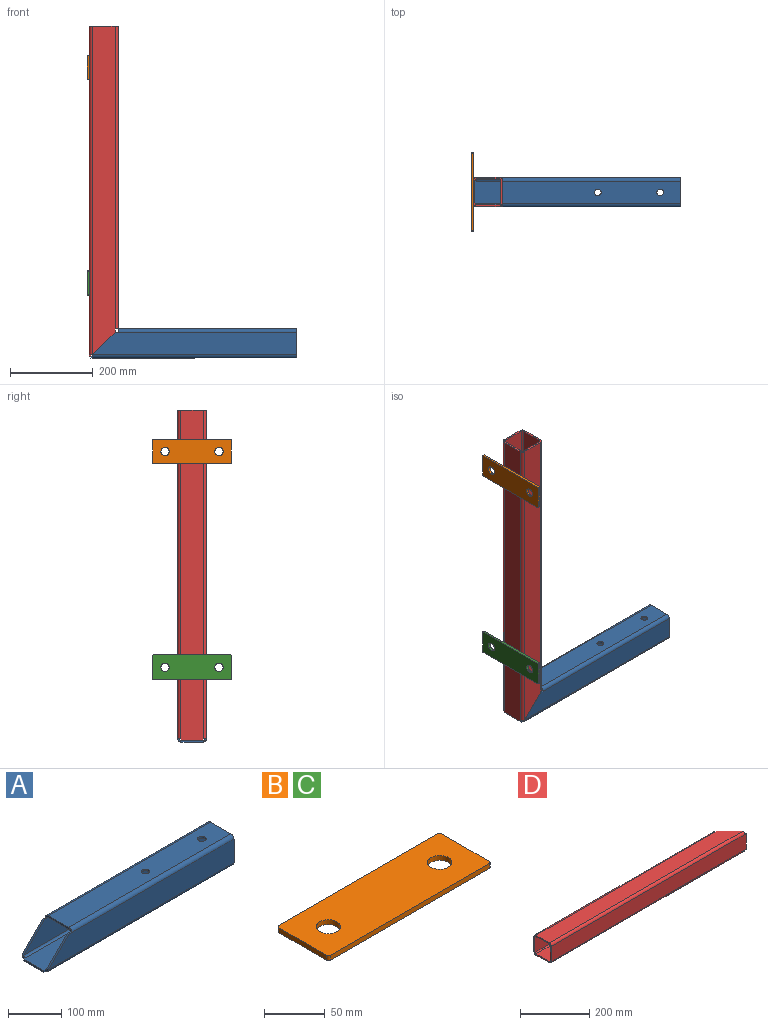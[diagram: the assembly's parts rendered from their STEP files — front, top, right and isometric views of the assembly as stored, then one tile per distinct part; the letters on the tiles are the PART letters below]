
ASSEMBLY  parts=4 mates=2
PART A: 40 faces, bbox 496x70x70 mm
  f0: plane 54x4mm, normal (1,0,0), area 216mm2, adj f3,f4,f32,f36
  f1: plane 8x4mm, normal (0,0,1), area 32mm2, adj f2,f3,f4,f33
  f2: plane 54x54mm, normal (-0.71,0,0.71), area 305.5mm2, adj f1,f3,f4,f37
  f3: plane 492x54mm, normal (0,-1,0), area 25110mm2, adj f0,f1,f2,f34,f38
  f4: plane 492x54mm, normal (0,1,0), area 25110mm2, adj f0,f1,f2,f35,f39
  f5: plane 4x4mm, normal (0,1,0), area 16mm2, adj f8,f11,f12,f28
  f6: plane 54x4mm, normal (1,0,0), area 216mm2, adj f11,f12,f29,f36
  f7: plane 4x4mm, normal (0,-1,0), area 16mm2, adj f8,f11,f12,f37
  f8: plane 54x4mm, normal (-1,0,0), area 216mm2, adj f5,f7,f11,f12
  f9: cylinder r=8mm len=16mm, axis (0,0,1), area 201.1mm2, adj f11,f12
  f10: cylinder r=8mm len=16mm, axis (0,0,1), area 201.1mm2, adj f11,f12
  f11: plane 496x54mm, normal (0,0,-1), area 26381.9mm2, adj f5,f6,f7,f8,f9,f10,f30,f38
  f12: plane 496x54mm, normal (0,0,1), area 26381.9mm2, adj f5,f6,f7,f8,f9,f10,f31,f39
  f13: plane 54x4mm, normal (1,0,0), area 216mm2, adj f17,f18,f25,f32
  f14: cylinder r=8mm len=16mm, axis (0,0,1), area 201.1mm2, adj f17,f18
  f15: cylinder r=8mm len=16mm, axis (0,0,1), area 201.1mm2, adj f17,f18
  f16: plane 54x4mm, normal (-1,0,0), area 216mm2, adj f17,f18,f24,f33
  f17: plane 430x54mm, normal (0,0,1), area 22817.9mm2, adj f13,f14,f15,f16,f26,f34
  f18: plane 430x54mm, normal (0,0,-1), area 22817.9mm2, adj f13,f14,f15,f16,f27,f35
  f19: plane 8x4mm, normal (0,0,1), area 32mm2, adj f21,f22,f23,f24
  f20: plane 54x4mm, normal (1,0,0), area 216mm2, adj f22,f23,f25,f29
  f21: plane 54x54mm, normal (-0.71,0,0.71), area 305.5mm2, adj f19,f22,f23,f28
  f22: plane 492x54mm, normal (0,1,0), area 25110mm2, adj f19,f20,f21,f26,f30
  f23: plane 492x54mm, normal (0,-1,0), area 25110mm2, adj f19,f20,f21,f27,f31
  f24: plane 8x8mm, normal (-1,0,0), area 37.7mm2, adj f16,f19,f26,f27
  f25: plane 8x8mm, normal (1,0,0), area 37.7mm2, adj f13,f20,f26,f27
  f26: cylinder r=8mm len=430mm, axis (-1,0,0), area 5403.5mm2, adj f17,f22,f24,f25
  f27: cylinder r=4mm len=430mm, axis (-1,0,0), area 2701.8mm2, adj f18,f23,f24,f25
  f28: plane 8x8mm, normal (-1,0,0), area 37.7mm2, adj f5,f21,f30,f31
  f29: plane 8x8mm, normal (1,0,0), area 37.7mm2, adj f6,f20,f30,f31
  f30: cylinder r=8mm len=492mm, axis (-1,0,0), area 6182.7mm2, adj f11,f22,f28,f29
  f31: cylinder r=4mm len=492mm, axis (-1,0,0), area 3091.3mm2, adj f12,f23,f28,f29
  f32: plane 8x8mm, normal (1,0,0), area 37.7mm2, adj f0,f13,f34,f35
  f33: plane 8x8mm, normal (-1,0,0), area 37.7mm2, adj f1,f16,f34,f35
  f34: cylinder r=8mm len=430mm, axis (1,0,0), area 5403.5mm2, adj f3,f17,f32,f33
  f35: cylinder r=4mm len=430mm, axis (1,0,0), area 2701.8mm2, adj f4,f18,f32,f33
  f36: plane 8x8mm, normal (1,0,0), area 37.7mm2, adj f0,f6,f38,f39
  f37: plane 8x8mm, normal (-1,0,0), area 37.7mm2, adj f2,f7,f38,f39
  f38: cylinder r=8mm len=492mm, axis (1,0,0), area 6182.7mm2, adj f3,f11,f36,f37
  f39: cylinder r=4mm len=492mm, axis (1,0,0), area 3091.3mm2, adj f4,f12,f36,f37
PART B: 12 faces, bbox 190x60x5 mm
  f0: plane 190x60mm, normal (0,0,1), area 10768.2mm2, adj f2,f3,f4,f5,f6,f7,f8,f9
  f1: plane 190x60mm, normal (0,0,-1), area 10768.2mm2, adj f2,f3,f4,f5,f6,f7,f8,f9
  f2: plane 56x5mm, normal (-1,0,0), area 280mm2, adj f0,f1,f8,f11
  f3: plane 186x5mm, normal (0,-1,0), area 930mm2, adj f0,f1,f8,f9
  f4: plane 56x5mm, normal (1,0,0), area 280mm2, adj f0,f1,f9,f10
  f5: plane 186x5mm, normal (0,1,0), area 930mm2, adj f0,f1,f10,f11
  f6: cylinder r=10mm len=20mm, axis (0,0,-1), area 314.2mm2, adj f0,f1
  f7: cylinder r=10mm len=20mm, axis (0,0,-1), area 314.2mm2, adj f0,f1
  f8: cylinder r=2mm len=5mm, axis (0,0,-1), area 15.7mm2, adj f0,f1,f2,f3
  f9: cylinder r=2mm len=5mm, axis (0,0,-1), area 15.7mm2, adj f0,f1,f3,f4
  f10: cylinder r=2mm len=5mm, axis (0,0,-1), area 15.7mm2, adj f0,f1,f4,f5
  f11: cylinder r=2mm len=5mm, axis (0,0,-1), area 15.7mm2, adj f0,f1,f2,f5
PART C: same geometry as B
PART D: 36 faces, bbox 796x70x70 mm
  f0: plane 4x4mm, normal (0,0,1), area 16mm2, adj f3,f4,f5,f28
  f1: plane 54x4mm, normal (-1,0,0), area 216mm2, adj f4,f5,f29,f33
  f2: plane 4x4mm, normal (0,0,-1), area 16mm2, adj f3,f4,f5,f32
  f3: plane 54x4mm, normal (1,0,0), area 216mm2, adj f0,f2,f4,f5
  f4: plane 796x54mm, normal (0,-1,0), area 42984mm2, adj f0,f1,f2,f3,f30,f34
  f5: plane 796x54mm, normal (0,1,0), area 42984mm2, adj f0,f1,f2,f3,f31,f35
  f6: plane 54x4mm, normal (-1,0,0), area 216mm2, adj f9,f10,f24,f33
  f7: plane 8x4mm, normal (0,1,0), area 32mm2, adj f8,f9,f10,f25
  f8: plane 54x54mm, normal (0.71,0.71,0), area 305.5mm2, adj f7,f9,f10,f32
  f9: plane 792x54mm, normal (0,0,-1), area 41310mm2, adj f6,f7,f8,f26,f34
  f10: plane 792x54mm, normal (0,0,1), area 41310mm2, adj f6,f7,f8,f27,f35
  f11: plane 8x4mm, normal (0,1,0), area 32mm2, adj f13,f14,f15,f21
  f12: plane 54x4mm, normal (-1,0,0), area 216mm2, adj f14,f15,f20,f29
  f13: plane 54x54mm, normal (0.71,0.71,0), area 305.5mm2, adj f11,f14,f15,f28
  f14: plane 792x54mm, normal (0,0,1), area 41310mm2, adj f11,f12,f13,f22,f30
  f15: plane 792x54mm, normal (0,0,-1), area 41310mm2, adj f11,f12,f13,f23,f31
  f16: plane 54x4mm, normal (-1,0,0), area 216mm2, adj f18,f19,f20,f24
  f17: plane 54x4mm, normal (1,0,0), area 216mm2, adj f18,f19,f21,f25
  f18: plane 730x54mm, normal (0,1,0), area 39420mm2, adj f16,f17,f22,f26
  f19: plane 730x54mm, normal (0,-1,0), area 39420mm2, adj f16,f17,f23,f27
  f20: plane 8x8mm, normal (-1,0,0), area 37.7mm2, adj f12,f16,f22,f23
  f21: plane 8x8mm, normal (1,0,0), area 37.7mm2, adj f11,f17,f22,f23
  f22: cylinder r=8mm len=730mm, axis (-1,0,0), area 9173.5mm2, adj f14,f18,f20,f21
  f23: cylinder r=4mm len=730mm, axis (-1,0,0), area 4586.7mm2, adj f15,f19,f20,f21
  f24: plane 8x8mm, normal (-1,0,0), area 37.7mm2, adj f6,f16,f26,f27
  f25: plane 8x8mm, normal (1,0,0), area 37.7mm2, adj f7,f17,f26,f27
  f26: cylinder r=8mm len=730mm, axis (-1,0,0), area 9173.5mm2, adj f9,f18,f24,f25
  f27: cylinder r=4mm len=730mm, axis (-1,0,0), area 4586.7mm2, adj f10,f19,f24,f25
  f28: plane 8x8mm, normal (1,0,0), area 37.7mm2, adj f0,f13,f30,f31
  f29: plane 8x8mm, normal (-1,0,0), area 37.7mm2, adj f1,f12,f30,f31
  f30: cylinder r=8mm len=792mm, axis (1,0,0), area 9952.6mm2, adj f4,f14,f28,f29
  f31: cylinder r=4mm len=792mm, axis (1,0,0), area 4976.3mm2, adj f5,f15,f28,f29
  f32: plane 8x8mm, normal (1,0,0), area 37.7mm2, adj f2,f8,f34,f35
  f33: plane 8x8mm, normal (-1,0,0), area 37.7mm2, adj f1,f6,f34,f35
  f34: cylinder r=8mm len=792mm, axis (1,0,0), area 9952.6mm2, adj f4,f9,f32,f33
  f35: cylinder r=4mm len=792mm, axis (1,0,0), area 4976.3mm2, adj f5,f10,f32,f33
PLACE A t=(-60.12,-14.4,-180.87)mm
PLACE B rot(axis=(0.58,0.58,0.58),120deg) t=(-261.01,-8.55,511.56)mm
PLACE C rot(axis=(0.58,0.58,0.58),120deg) t=(-261.01,-8.55,-8.44)mm
PLACE D rot(axis=(0.58,0.58,-0.58),120deg) t=(-231.85,35.54,483.24)mm
MATE parallel D.f4 <-> B.f0  axis (-1,0,0) through (-255.78,0.54,619.13)mm
MATE parallel D.f13 <-> A.f2  axis (0.71,0,-0.71) through (-220.78,-32.46,-145.87)mm
